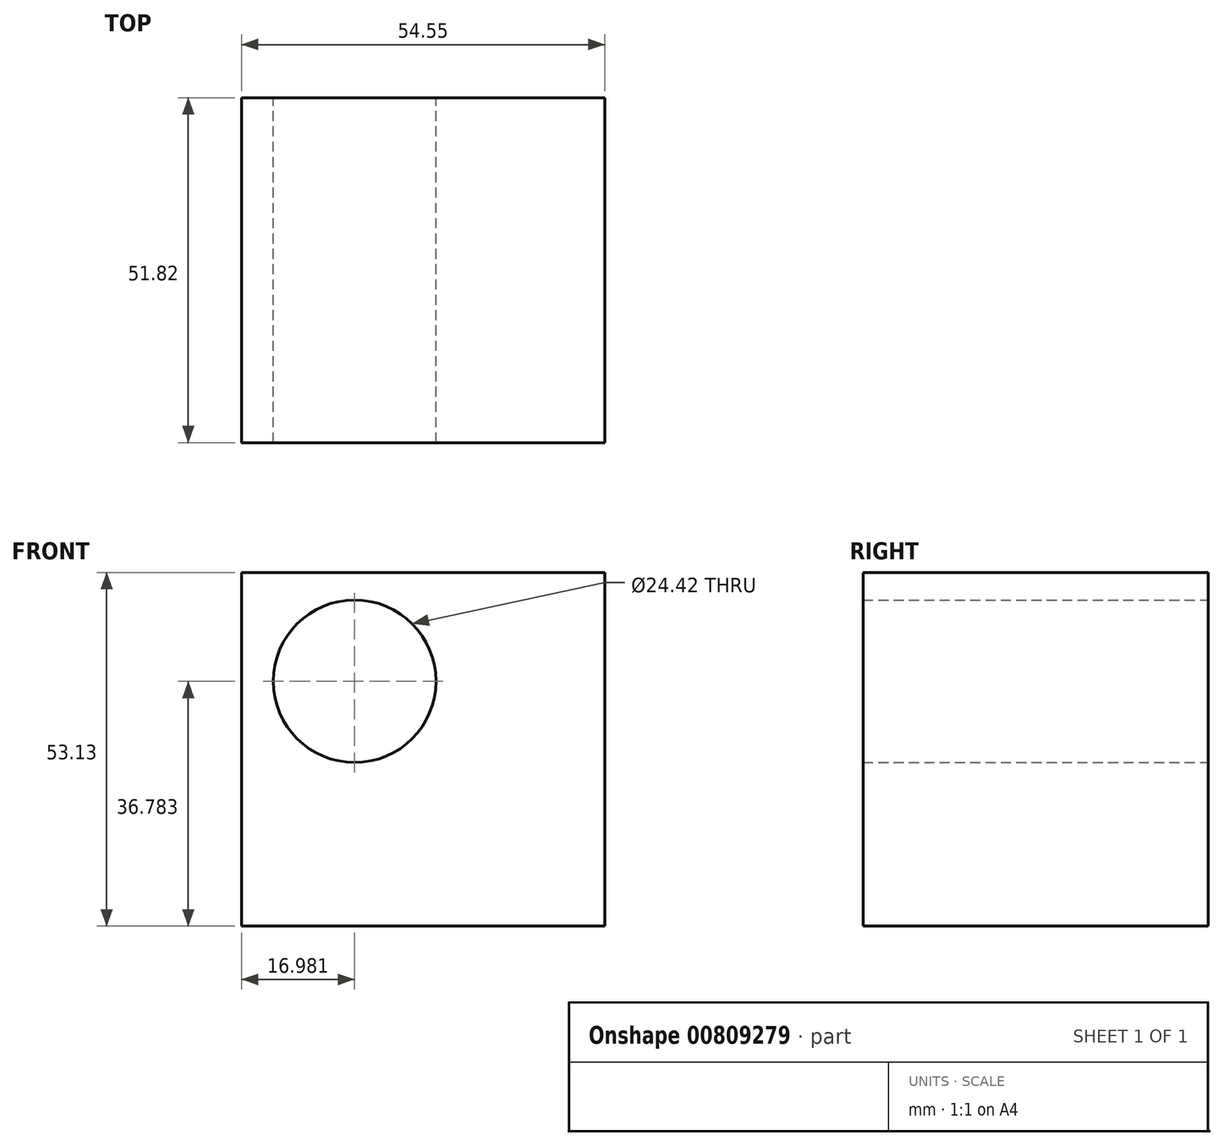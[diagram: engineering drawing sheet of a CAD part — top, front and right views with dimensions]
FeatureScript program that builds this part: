
annotation { "Feature Type Name" : "Feature", "Feature Type Description" : "" }
export const myFeature = defineFeature(function(context is Context, id is Id, definition is map)
    precondition{}
    {
        {
            var Q0;
            Q0=qCreatedBy(makeId("Front.planeOp"),FACE);
            var sketch = newSketch(context, id + "F0", { "sketchPlane" : qUnion([Q0])});
            skLineSegment(sketch, "E0", {"start": v(-4.24, 0) * mm, "end": v(-54.55, 0) * mm});
            skLineSegment(sketch, "E1", {"start": v(-54.55, 0) * mm, "end": v(-54.55, 53.13) * mm});
            skLineSegment(sketch, "E2", {"start": v(-54.55, 53.13) * mm, "end": v(0, 53.13) * mm});
            skLineSegment(sketch, "E3", {"start": v(0, 53.13) * mm, "end": v(0, 0) * mm});
            skLineSegment(sketch, "E4", {"start": v(0, 0) * mm, "end": v(-4.24, 0) * mm});
            skSolve(sketch);
        }
        {
            var Q0;
            Q0=makeQuery(id+"F0.imprint","IMPRINT",FACE,{"disambiguationData":[TD([[makeQuery(id+"F0.imprint","IMPRINT",EDGE,{"derivedFrom":sQuery(id+"F0.wireOp",EDGE,"E0")}),-1.0]])]});
            extrude(context, id + "F1", {"entities" : qUnion([Q0]), "depth" : 51.82 * mm, "offsetDistance" : 25.4 * mm});
        }
        {
            var Q0;
            Q0=qCreatedBy(makeId("Front.planeOp"),FACE);
            var sketch = newSketch(context, id + "F2", { "sketchPlane" : qUnion([Q0])});
            skCircle(sketch, "E5", {"center": v(-37.57, 36.78) * mm, "radius": 12.2 * mm});
            skSolve(sketch);
        }
        {
            var Q0;
            Q0=makeQuery(id+"F2.imprint","IMPRINT",FACE,{"disambiguationData":[TD([[makeQuery(id+"F2.imprint","IMPRINT",EDGE,{"derivedFrom":sQuery(id+"F2.wireOp",EDGE,"E5")}),1.0]])]});
            extrude(context, id + "F3", {"entities" : qUnion([Q0]), "operationType" : NewBodyOperationType.REMOVE, "depth" : 129.29 * mm, "offsetDistance" : 25.4 * mm});
        }
    });
